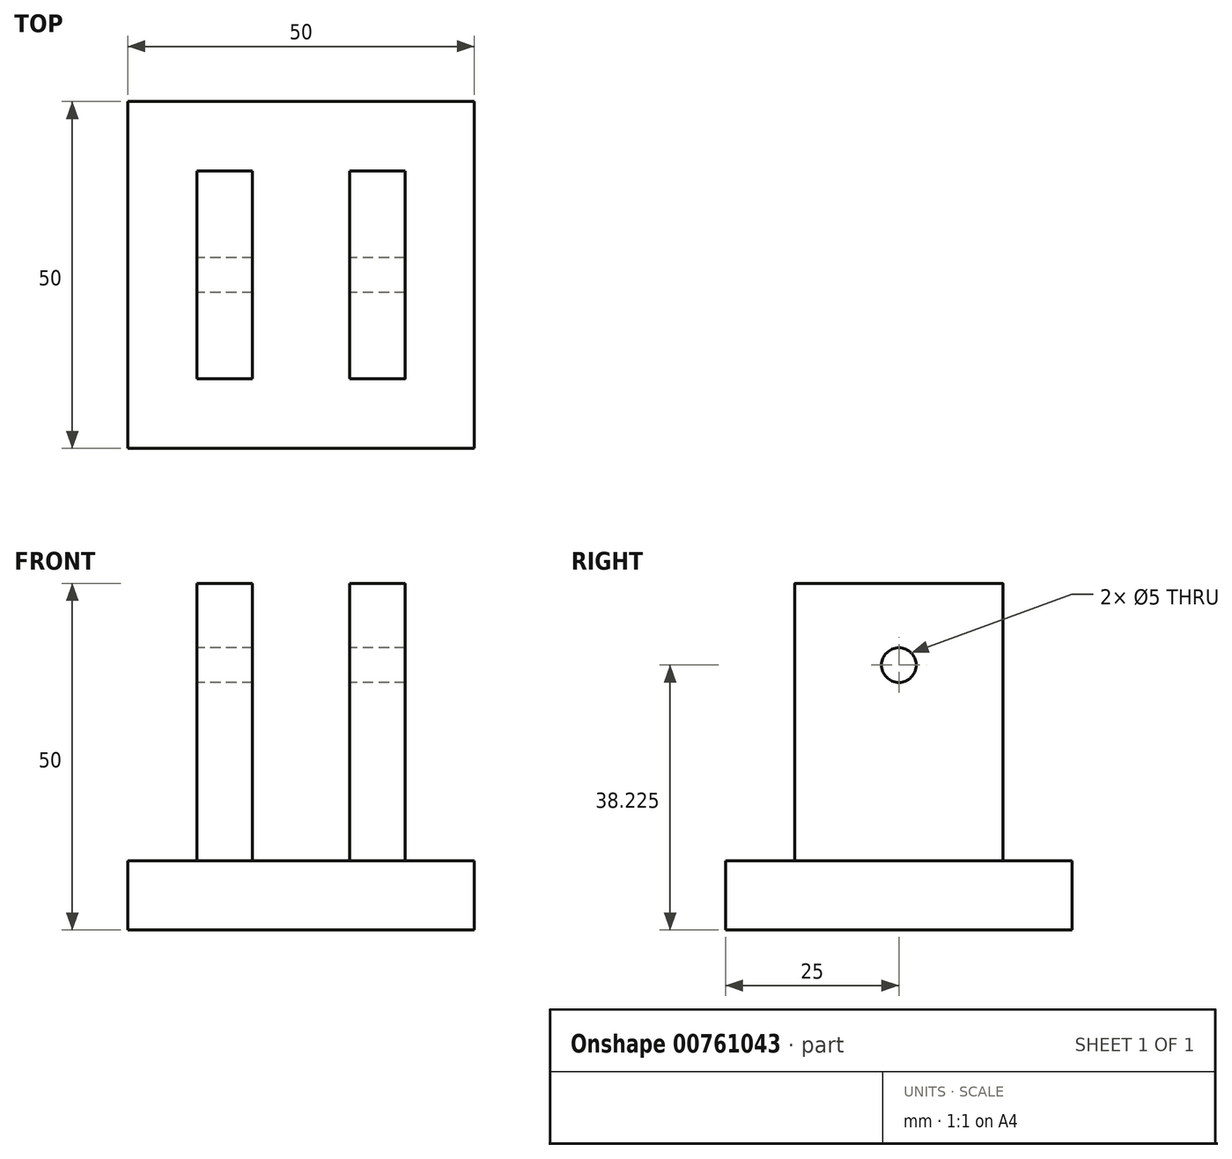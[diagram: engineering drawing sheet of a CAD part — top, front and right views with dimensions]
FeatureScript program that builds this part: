
annotation { "Feature Type Name" : "Feature", "Feature Type Description" : "" }
export const myFeature = defineFeature(function(context is Context, id is Id, definition is map)
    precondition{}
    {
        {
            var Q0;
            Q0=qCreatedBy(makeId("Top.planeOp"),FACE);
            var sketch = newSketch(context, id + "F0", { "sketchPlane" : qUnion([Q0])});
            skLineSegment(sketch, "E0.bottom", {"start": v(0, 0) * mm, "end": v(50, 0) * mm});
            skLineSegment(sketch, "E0.top", {"start": v(0, -50) * mm, "end": v(50, -50) * mm});
            skLineSegment(sketch, "E0.left", {"start": v(0, 0) * mm, "end": v(0, -50) * mm});
            skLineSegment(sketch, "E0.right", {"start": v(50, 0) * mm, "end": v(50, -50) * mm});
            skSolve(sketch);
        }
        {
            var Q0;
            Q0=makeQuery(id+"F0.imprint","IMPRINT",FACE,{"disambiguationData":[TD([[makeQuery(id+"F0.imprint","IMPRINT",EDGE,{"derivedFrom":sQuery(id+"F0.wireOp",EDGE,"E0.bottom")}),-1.0]])]});
            extrude(context, id + "F1", {"entities" : qUnion([Q0]), "depth" : 10 * mm, "offsetDistance" : 25 * mm});
        }
        {
            var Q0;
            Q0=makeQuery(id+"F1.opExtrude","CAP_FACE",FACE,{"disambiguationData":[OSD([sQuery(id+"F0.wireOp",EDGE,"E0.bottom"),sQuery(id+"F0.wireOp",EDGE,"E0.top"),sQuery(id+"F0.wireOp",EDGE,"E0.left"),sQuery(id+"F0.wireOp",EDGE,"E0.right")])],"isStart":false});
            var sketch = newSketch(context, id + "F2", { "sketchPlane" : qUnion([Q0])});
            skLineSegment(sketch, "E1.bottom", {"start": v(10, -10) * mm, "end": v(18, -10) * mm});
            skLineSegment(sketch, "E1.top", {"start": v(10, -40) * mm, "end": v(18, -40) * mm});
            skLineSegment(sketch, "E1.left", {"start": v(10, -10) * mm, "end": v(10, -40) * mm});
            skLineSegment(sketch, "E1.right", {"start": v(18, -10) * mm, "end": v(18, -40) * mm});
            skLineSegment(sketch, "E2.bottom", {"start": v(32, -10) * mm, "end": v(40, -10) * mm});
            skLineSegment(sketch, "E2.top", {"start": v(32, -40) * mm, "end": v(40, -40) * mm});
            skLineSegment(sketch, "E2.left", {"start": v(32, -10) * mm, "end": v(32, -40) * mm});
            skLineSegment(sketch, "E2.right", {"start": v(40, -10) * mm, "end": v(40, -40) * mm});
            skSolve(sketch);
        }
        {
            var Q0;
            Q0 = qSketchRegion(id + "F2", true);
            extrude(context, id + "F3", {"entities" : qUnion([Q0]), "operationType" : NewBodyOperationType.ADD, "depth" : 40 * mm, "offsetDistance" : 25 * mm});
        }
        {
            var Q0;
            Q0=makeQuery(id+"F3.opExtrude","SWEPT_FACE",FACE,{"disambiguationData":[OSD([sQuery(id+"F2.wireOp",EDGE,"E1.left")])]});
            var sketch = newSketch(context, id + "F4", { "sketchPlane" : qUnion([Q0])});
            skPoint(sketch, "E3", {"position": v(25, 38.23) * mm});
            skPoint(sketch, "E3.positionSnap0", {"position": v(25, 50) * mm});
            skSolve(sketch);
        }
        {
            var Q0;
            Q0=sQuery(id+"F4.wireOp",VERTEX,"E3");
            var Q1;
            Q1=makeQuery(id+"F1.opExtrude","SWEPT_BODY",BODY,{"disambiguationData":[OSD([sQuery(id+"F0.wireOp",EDGE,"E0.bottom"),sQuery(id+"F0.wireOp",EDGE,"E0.top"),sQuery(id+"F0.wireOp",EDGE,"E0.left"),sQuery(id+"F0.wireOp",EDGE,"E0.right")])]});
            hole(context, id + "F5", {"style" : HoleStyle.SIMPLE, "endStyle" : HoleEndStyle.THROUGH, "holeDiameter" : 5 * mm, "majorDiameter" : 5 * mm, "isTappedThrough" : true, "tappedDepth" : 12 * mm, "tapClearance" : 3, "locations" : qUnion([Q0]), "scope" : qUnion([Q1])});
        }
        {
            var Q0;
            Q0=makeQuery(id+"F3.opExtrude","CAP_EDGE",EDGE,{"disambiguationData":[OSD([sQuery(id+"F2.wireOp",EDGE,"E2.right")])],"isStart":false});
            fillet(context, id + "F6", {"entities" : qUnion([Q0]), "radius" : 0.02 * mm, "tangentPropagation" : true, "allowEdgeOverflow" : false});
        }
    });
